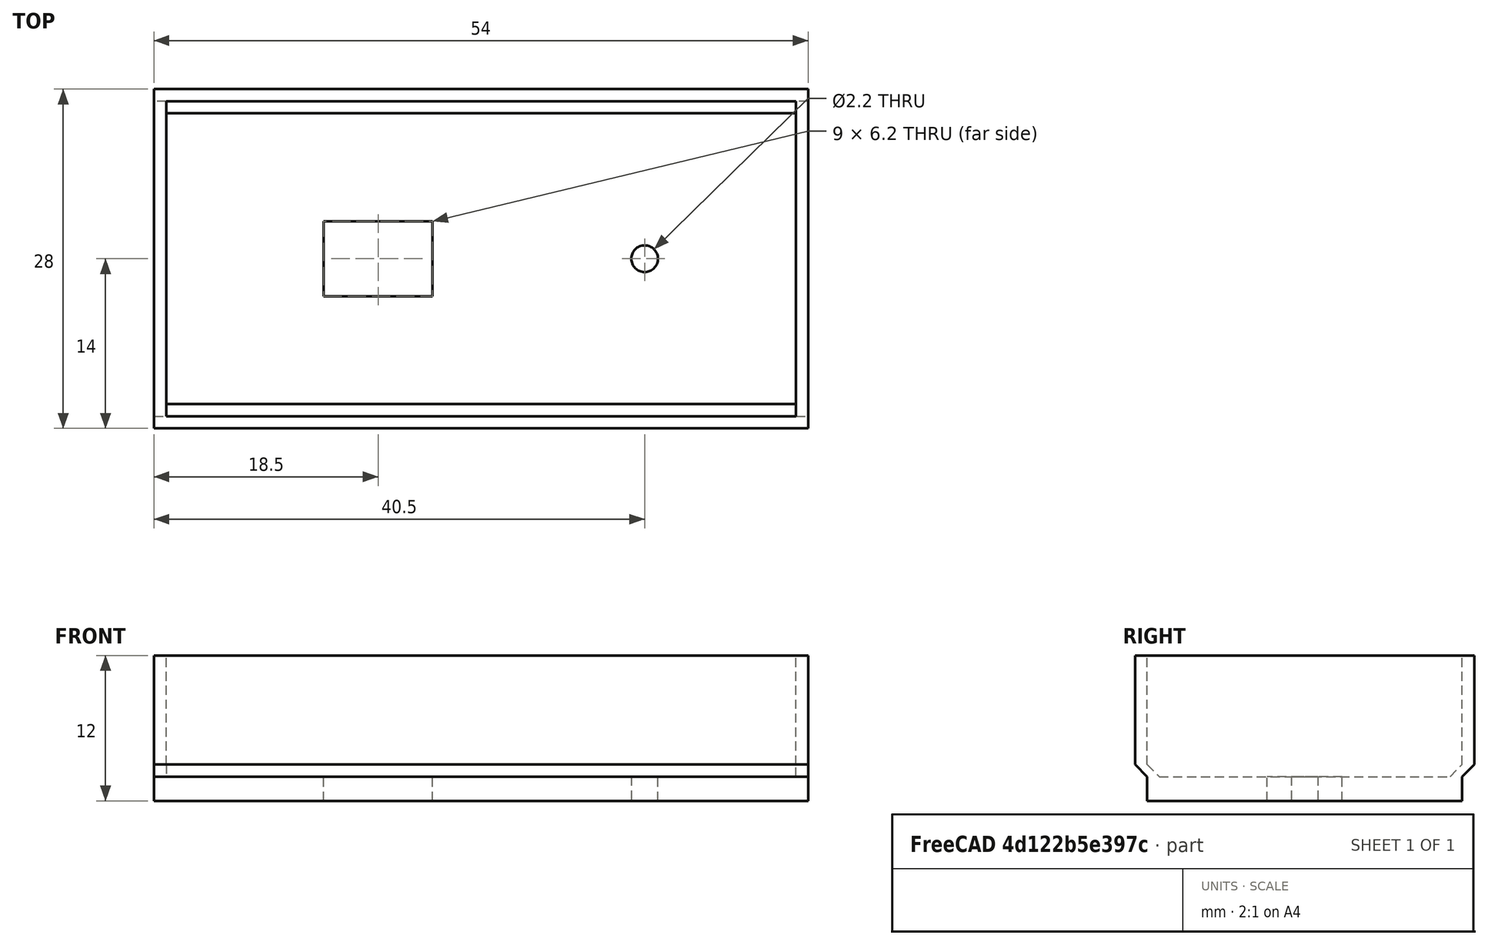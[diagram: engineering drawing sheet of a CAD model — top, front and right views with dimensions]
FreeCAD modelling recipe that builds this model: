
FCSTD DOCUMENT  (FreeCAD 0.20RUnknown)
Label: MatchboxLadeflaeche
License: All rights reserved
LicenseURL: http://en.wikipedia.org/wiki/All_rights_reserved
objects: Sketcher::SketchObject×4, PartDesign::Pad×3, PartDesign::Pocket×1, PartDesign::Body×1
note: 13 computed .brp shape members not serialized (recipe doc carries the construction recipe); baked Part::Feature solids carry a one-line shape summary decoded from their .brp

FEATURE [Sketcher::SketchObject] Sketch
  FullyConstrained = true
  MapMode = 5
  Support = -> [XY_Plane]
  sketch-geometry (13):
    g0: LineSegment StartX=0 StartY=0 StartZ=0 EndX=54 EndY=0 EndZ=0
    g1: LineSegment StartX=54 StartY=0 StartZ=0 EndX=54 EndY=26 EndZ=0
    g2: LineSegment StartX=54 StartY=26 StartZ=0 EndX=0 EndY=26 EndZ=0
    g3: LineSegment StartX=0 StartY=26 StartZ=0 EndX=0 EndY=0 EndZ=0
    g4: LineSegment StartX=14 StartY=16.1 StartZ=0 EndX=23 EndY=16.1 EndZ=0
    g5: LineSegment StartX=23 StartY=16.1 StartZ=0 EndX=23 EndY=9.9 EndZ=0
    g6: LineSegment StartX=23 StartY=9.9 StartZ=0 EndX=14 EndY=9.9 EndZ=0
    g7: LineSegment StartX=14 StartY=9.9 StartZ=0 EndX=14 EndY=16.1 EndZ=0
    g8: Circle CenterX=40.5 CenterY=13 CenterZ=0 NormalX=0 NormalY=0 NormalZ=1 AngleXU=0 Radius=1.1
    g9: LineSegment StartX=40.5 StartY=13 StartZ=0 EndX=40.5 EndY=26 EndZ=0
    g10: LineSegment StartX=40.5 StartY=13 StartZ=0 EndX=40.5 EndY=0 EndZ=0
    g11: LineSegment StartX=23 StartY=16.1 StartZ=0 EndX=23 EndY=26 EndZ=0
    g12: LineSegment StartX=23 StartY=9.9 StartZ=0 EndX=23 EndY=0 EndZ=0
  constraints (38):
    c: Coincident(g0,g1)
    c: Coincident(g1,g2)
    c: Coincident(g2,g3)
    c: Coincident(g3,g0)
    c: Horizontal(g0)
    c: Horizontal(g2)
    c: Vertical(g1)
    c: Vertical(g3)
    c: Coincident(g0,g-1)
    c: Coincident(g4,g5)
    c: Coincident(g5,g6)
    c: Coincident(g6,g7)
    c: Coincident(g7,g4)
    c: Horizontal(g4)
    c: Horizontal(g6)
    c: Vertical(g5)
    c: Vertical(g7)
    c: DistanceX(g2,g2) = 54
    c: DistanceY(g1,g1) = 26
    c: DistanceX(g2,g4) = 14
    c: DistanceX(g4,g4) = 9
    c: DistanceY(g5,g5) = 6.2
    c: DistanceX(g2,g8) = 40.5
    c: Diameter(g8) = 2.2
    c: Coincident(g9,g8)
    c: PointOnObject(g9,g2)
    c: Vertical(g9)
    c: Coincident(g10,g8)
    c: PointOnObject(g10,g0)
    c: Vertical(g10)
    c: Equal(g9,g10)
    c: Coincident(g11,g4)
    c: PointOnObject(g11,g2)
    c: Vertical(g11)
    c: Coincident(g12,g5)
    c: PointOnObject(g12,g0)
    c: Vertical(g12)
    c: Equal(g12,g11)
FEATURE [PartDesign::Pad] Pad
  Direction = (0,0,1)
  Length = 2
  Length2 = 10
  Profile = -> Sketch
  ReferenceAxis = -> Sketch [N_Axis]
  Type = 0
FEATURE [Sketcher::SketchObject] Sketch001
  ExternalGeometry = -> [Pad]
  FullyConstrained = true
  MapMode = 5
  Placement = pos=(0,0,2) rot=(0,0,1;0rad)
  Support = -> [Pad]
  sketch-geometry (14):
    g0: LineSegment StartX=0 StartY=27 StartZ=0 EndX=54 EndY=27 EndZ=0
    g1: LineSegment StartX=54 StartY=27 StartZ=0 EndX=54 EndY=-1 EndZ=0
    g2: LineSegment StartX=54 StartY=-1 StartZ=0 EndX=0 EndY=-1 EndZ=0
    g3: LineSegment StartX=0 StartY=-1 StartZ=0 EndX=0 EndY=27 EndZ=0
    g4: LineSegment StartX=54 StartY=26 StartZ=0 EndX=54 EndY=27 EndZ=0
    g5: LineSegment StartX=54 StartY=0 StartZ=0 EndX=54 EndY=-1 EndZ=0
    g6: LineSegment StartX=1 StartY=26 StartZ=0 EndX=53 EndY=26 EndZ=0
    g7: LineSegment StartX=53 StartY=26 StartZ=0 EndX=53 EndY=0 EndZ=0
    g8: LineSegment StartX=53 StartY=9e-16 StartZ=0 EndX=1 EndY=9e-16 EndZ=0
    g9: LineSegment StartX=1 StartY=9e-16 StartZ=0 EndX=1 EndY=26 EndZ=0
    g10: LineSegment StartX=0 StartY=26 StartZ=0 EndX=1 EndY=26 EndZ=0
    g11: LineSegment StartX=1 StartY=26 StartZ=0 EndX=1 EndY=27 EndZ=0
    g12: LineSegment StartX=53 StartY=-1 StartZ=0 EndX=53 EndY=9e-16 EndZ=0
    g13: LineSegment StartX=53 StartY=9e-16 StartZ=0 EndX=54 EndY=9e-16 EndZ=0
  constraints (40):
    c: Coincident(g0,g1)
    c: Coincident(g1,g2)
    c: Coincident(g2,g3)
    c: Coincident(g3,g0)
    c: Horizontal(g0)
    c: Horizontal(g2)
    c: Vertical(g1)
    c: Vertical(g3)
    c: PointOnObject(g0,g-2)
    c: Coincident(g4,g-3)
    c: Coincident(g4,g0)
    c: Coincident(g5,g-4)
    c: Coincident(g5,g1)
    c: Equal(g4,g5)
    c: Vertical(g4)
    c: Coincident(g6,g7)
    c: Coincident(g7,g8)
    c: Coincident(g8,g9)
    c: Coincident(g9,g6)
    c: Horizontal(g6)
    c: Horizontal(g8)
    c: Vertical(g7)
    c: Vertical(g9)
    c: PointOnObject(g10,g3)
    c: Coincident(g10,g6)
    c: Coincident(g10,g11)
    c: PointOnObject(g11,g0)
    c: Vertical(g11)
    c: PointOnObject(g12,g2)
    c: Coincident(g12,g7)
    c: Coincident(g12,g13)
    c: PointOnObject(g13,g1)
    c: Horizontal(g13)
    c: Vertical(g12)
    c: Equal(g12,g13)
    c: Equal(g11,g10)
    c: Horizontal(g10)
    c: Equal(g11,g12)
    c: DistanceX(g13,g13) = 1
    c: DistanceY(g1,g0) = 28
FEATURE [PartDesign::Pad] Pad001
  BaseFeature = -> Pad
  Direction = (0,0,1)
  Length = 10
  Length2 = 10
  Profile = -> Sketch001
  ReferenceAxis = -> Sketch001 [N_Axis]
  Type = 0
FEATURE [Sketcher::SketchObject] Sketch002
  ExternalGeometry = -> [Pad001]
  FullyConstrained = true
  MapMode = 5
  Placement = pos=(1,0,0) rot=(0.57735,0.57735,0.57735;2.0944rad)
  Support = -> [Pad001]
  sketch-geometry (6):
    g0: LineSegment StartX=9e-16 StartY=2 StartZ=0 EndX=9e-16 EndY=3 EndZ=0
    g1: LineSegment StartX=9e-16 StartY=3 StartZ=0 EndX=1 EndY=2 EndZ=0
    g2: LineSegment StartX=1 StartY=2 StartZ=0 EndX=9e-16 EndY=2 EndZ=0
    g3: LineSegment StartX=26 StartY=2 StartZ=0 EndX=26 EndY=3 EndZ=0
    g4: LineSegment StartX=26 StartY=3 StartZ=0 EndX=25 EndY=2 EndZ=0
    g5: LineSegment StartX=25 StartY=2 StartZ=0 EndX=26 EndY=2 EndZ=0
  constraints (16):
    c: Coincident(g5,g3)
    c: Coincident(g-3,g3)
    c: Horizontal(g5)
    c: Coincident(g5,g4)
    c: Coincident(g3,g4)
    c: Vertical(g3)
    c: Equal(g3,g5)
    c: Coincident(g2,g0)
    c: Coincident(g-3,g0)
    c: Coincident(g2,g1)
    c: Coincident(g0,g1)
    c: Vertical(g0)
    c: Horizontal(g2)
    c: Equal(g0,g2)
    c: Equal(g2,g5)
    c: DistanceY(g0,g0) = 1
FEATURE [PartDesign::Pad] Pad002
  BaseFeature = -> Pad001
  Direction = (1,0,0)
  Length = 10
  Length2 = 10
  Profile = -> Sketch002
  ReferenceAxis = -> Sketch002 [N_Axis]
  Type = 2
FEATURE [Sketcher::SketchObject] Sketch003
  ExternalGeometry = -> [Pad002]
  FullyConstrained = true
  MapMode = 5
  Placement = pos=(54,0,0) rot=(0.57735,0.57735,0.57735;2.0944rad)
  Support = -> [Pad002]
  sketch-geometry (6):
    g0: LineSegment StartX=-1 StartY=2 StartZ=0 EndX=-1 EndY=3 EndZ=0
    g1: LineSegment StartX=-1 StartY=3 StartZ=0 EndX=0 EndY=2 EndZ=0
    g2: LineSegment StartX=0 StartY=2 StartZ=0 EndX=-1 EndY=2 EndZ=0
    g3: LineSegment StartX=27 StartY=2 StartZ=0 EndX=27 EndY=3 EndZ=0
    g4: LineSegment StartX=27 StartY=3 StartZ=0 EndX=26 EndY=2 EndZ=0
    g5: LineSegment StartX=26 StartY=2 StartZ=0 EndX=27 EndY=2 EndZ=0
  constraints (14):
    c: Coincident(g-3,g0)
    c: Vertical(g0)
    c: Coincident(g0,g1)
    c: Coincident(g1,g-3)
    c: Coincident(g1,g2)
    c: Coincident(g2,g0)
    c: Coincident(g-4,g3)
    c: Vertical(g3)
    c: Coincident(g3,g4)
    c: Coincident(g4,g-4)
    c: Coincident(g4,g5)
    c: Coincident(g5,g3)
    c: Equal(g5,g3)
    c: Equal(g0,g2)
FEATURE [PartDesign::Pocket] Pocket
  BaseFeature = -> Pad002
  Direction = (-1,0,0)
  Length = 5
  Length2 = 5
  Profile = -> Sketch003
  ReferenceAxis = -> Sketch003 [N_Axis]
  Type = 1
FEATURE [PartDesign::Body] Body
  Group = -> [Sketch,Pad,Sketch001,Pad001,Sketch002,Pad002,Sketch003,Pocket]
  Origin = -> Origin
  Tip = -> Pocket
